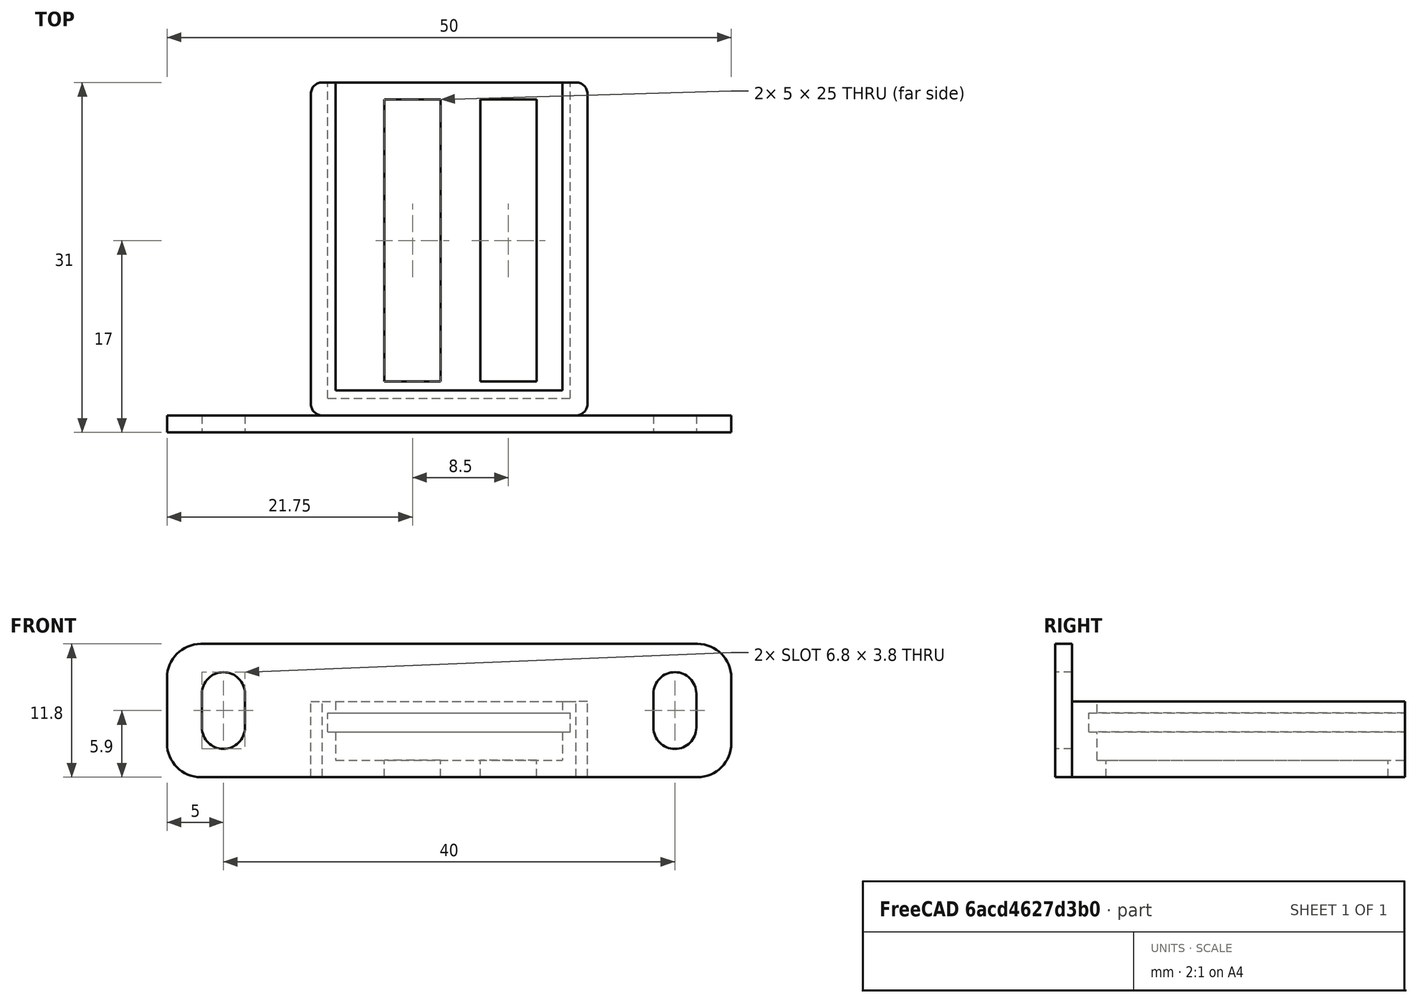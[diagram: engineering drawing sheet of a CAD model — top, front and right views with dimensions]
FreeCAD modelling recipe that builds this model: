
FCSTD DOCUMENT  (FreeCAD 0.19R23578 (Git))
Label: mcp23017_i2c_io_expansion
License: FreeArt
LicenseURL: http://artlibre.org/licence/lal
objects: Part::Box×5, Part::MultiFuse×3, Spreadsheet::Sheet×1, Part::Fillet×1, Part::Feature×1, Part::Cut×1, App::Part×1
note: 11 computed .brp shape members not serialized (recipe doc carries the construction recipe); baked Part::Feature solids carry a one-line shape summary decoded from their .brp

FEATURE [Spreadsheet::Sheet] Spreadsheet  label="p"
  cells = A1=pcb_x; B1(pcb_x)=21.5; A2=pcb_y; B2(pcb_y)=28; A3=pcb_z; B3(pcb_z)=1.7; A4=pcb_under; B4(pcb_under)=2.5; A5=side_wall; B5(side_wall)=1.5; A6=pcb_side_lane; B6(pcb_side_lane)=0.7; A7=bottom_wall; B7(bottom_wall)=1.5; A8=pcb_above; B8(pcb_above)=1; A9=view_hole_x; B9(view_hole_x)=5; A10=view_hole_y; B10(view_hole_y)=25; A11=hole_narrow_offset_x; B11(hole_narrow_offset_x)=3; A12=hole_wide_offset_x; B12(hole_wide_offset_x)=5
FEATURE [Part::Box] Box  label="external cube"
  AttacherType = Attacher::AttachEngine3D
  Height = 6.7
  Length = 24.5
  Width = 29.5
  expr: Length = <<p>>.pcb_x + 2 * <<p>>.side_wall
  expr: Width = <<p>>.pcb_y + <<p>>.side_wall
  expr: Height = <<p>>.bottom_wall + <<p>>.pcb_under + <<p>>.pcb_z + <<p>>.pcb_above
FEATURE [Part::Box] Box006  label="internal cube"
  AttacherType = Attacher::AttachEngine3D
  Height = 5.2
  Length = 20.1
  Placement = pos=(2.2,2.2,1.5) rot=(0,0,1;0rad)
  Width = 28.1
  expr: Length = <<p>>.pcb_x - 2 * <<p>>.pcb_side_lane
  expr: Width = <<p>>.pcb_y - 2 * <<p>>.pcb_side_lane + <<p>>.side_wall
  expr: Height = <<p>>.pcb_under + <<p>>.pcb_z + <<p>>.pcb_above
  expr: .Placement.Base.z = <<p>>.bottom_wall
  expr: .Placement.Base.x = <<p>>.side_wall + <<p>>.pcb_side_lane
  expr: .Placement.Base.y = <<p>>.side_wall + <<p>>.pcb_side_lane
FEATURE [Part::Box] Box007  label="pcb extract cube"
  AttacherType = Attacher::AttachEngine3D
  Height = 1.7
  Length = 21.5
  Placement = pos=(1.5,1.5,4) rot=(0,0,1;0rad)
  Width = 28
  expr: Height = <<p>>.pcb_z
  expr: .Placement.Base.z = <<p>>.bottom_wall + <<p>>.pcb_under
  expr: Width = <<p>>.pcb_y
  expr: Length = <<p>>.pcb_x
  expr: .Placement.Base.x = <<p>>.side_wall
  expr: .Placement.Base.y = <<p>>.side_wall
FEATURE [Part::Fillet] Fillet  label="external fillet"
  Base = -> Box
  Edges = 4 edges r=1: [Edge1,Edge3,Edge5,Edge7]
FEATURE [Part::Box] Box008  label="central view hole"
  AttacherType = Attacher::AttachEngine3D
  Height = 10
  Length = 5
  Placement = pos=(6.5,0,0) rot=(0,0,1;0rad)
  Width = 25
  expr: Length = <<p>>.view_hole_x
  expr: Width = <<p>>.view_hole_y
  expr: .Placement.Base.x = <<p>>.side_wall + <<p>>.hole_wide_offset_x
FEATURE [Part::Box] Box009  label="central view hole001"
  AttacherType = Attacher::AttachEngine3D
  Height = 10
  Length = 5
  Placement = pos=(15,0,0) rot=(0,0,1;0rad)
  Width = 25
  expr: Width = <<p>>.view_hole_y
  expr: Length = <<p>>.view_hole_x
  expr: .Placement.Base.x = <<p>>.side_wall + <<p>>.pcb_x - <<p>>.hole_narrow_offset_x - <<p>>.view_hole_x
FEATURE [Part::MultiFuse] Fusion002  label="view hole fusion"
  Placement = pos=(0,3,0) rot=(0,0,1;0rad)
  Shapes = -> [Box008,Box009]
  expr: .Placement.Base.y = <<p>>.side_wall + (<<p>>.pcb_y - <<p>>.view_hole_y) / 2
FEATURE [Part::MultiFuse] Fusion  label="extract fusion"
  Shapes = -> [Box006,Box007,Fusion002]
FEATURE [Part::Feature] Body002  label="attach plane x rotated dir001"
  Placement = pos=(-12.75,0,0) rot=(1,0,0;1.5708rad)
  shape: bbox 50 x 1.5 x 11.8 mm, 18 faces (baked)
FEATURE [Part::MultiFuse] Fusion001  label="body fusion"
  Shapes = -> [Fillet,Body002]
FEATURE [Part::Cut] Cut  label="body cut"
  Base = -> Fusion001
  Tool = -> Fusion
FEATURE [App::Part] Part  label="pcb box part"
  Group = -> [Box,Fillet,Fusion001,Fusion,Box007,Box006,Cut]
  Origin = -> Origin
